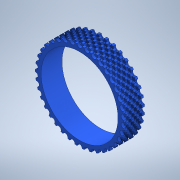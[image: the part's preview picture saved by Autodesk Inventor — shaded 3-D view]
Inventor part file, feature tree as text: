
AUTODESK INVENTOR PART (.ipt)
format: ipt  version: 2020 (Build 240168000, 168)  size: 1,092,608 bytes
history: native  units: in
note: dims shown in document units (in); Inventor stores cm internally (conversion verified against a paired STEP export)
features: extrude x3, sketch x3, pattern_circular x2, pattern_linear x1
ambient origin geometry x8: Origin, YZ Plane, XZ Plane, XY Plane, X Axis, Y Axis, Z Axis, Center Point
bodies: Solid1 (feature_tree)
feature tree (9):
  extrude  "Extrusion1"  Depth=1.0in
  extrude  "Extrusion2"  Depth=0.125in
  pattern_circular  "Circular Pattern3"  Count=38 Angle=360.0deg
  extrude  "Extrusion4"  Depth=0.125in
  pattern_circular  "Circular Pattern4"  [2 undecoded]
  pattern_linear  "Rectangular Pattern2"  Count1=38 Spacing1=360.0deg
  sketch  "Sketch1"  dims[d1=1.0in d2=0.0in d3=0.28in]
  sketch  "Sketch3"  dims[d4=3.685in d5=0.125in]
  sketch  "Sketch5"  dims[d6=0.125in d7=0.0in d27=14.9606in d28=360.0deg d30=0.125in d31=0.125in d32=0.0in d33=14.9606in d34=360.0deg d36=1.5748in d38=0.25in]
note: 2 required parameter values undecoded (feature->parameter linkage not recoverable at this tier; creation-order binding heuristic only, values carry confidence <= 0.55)
